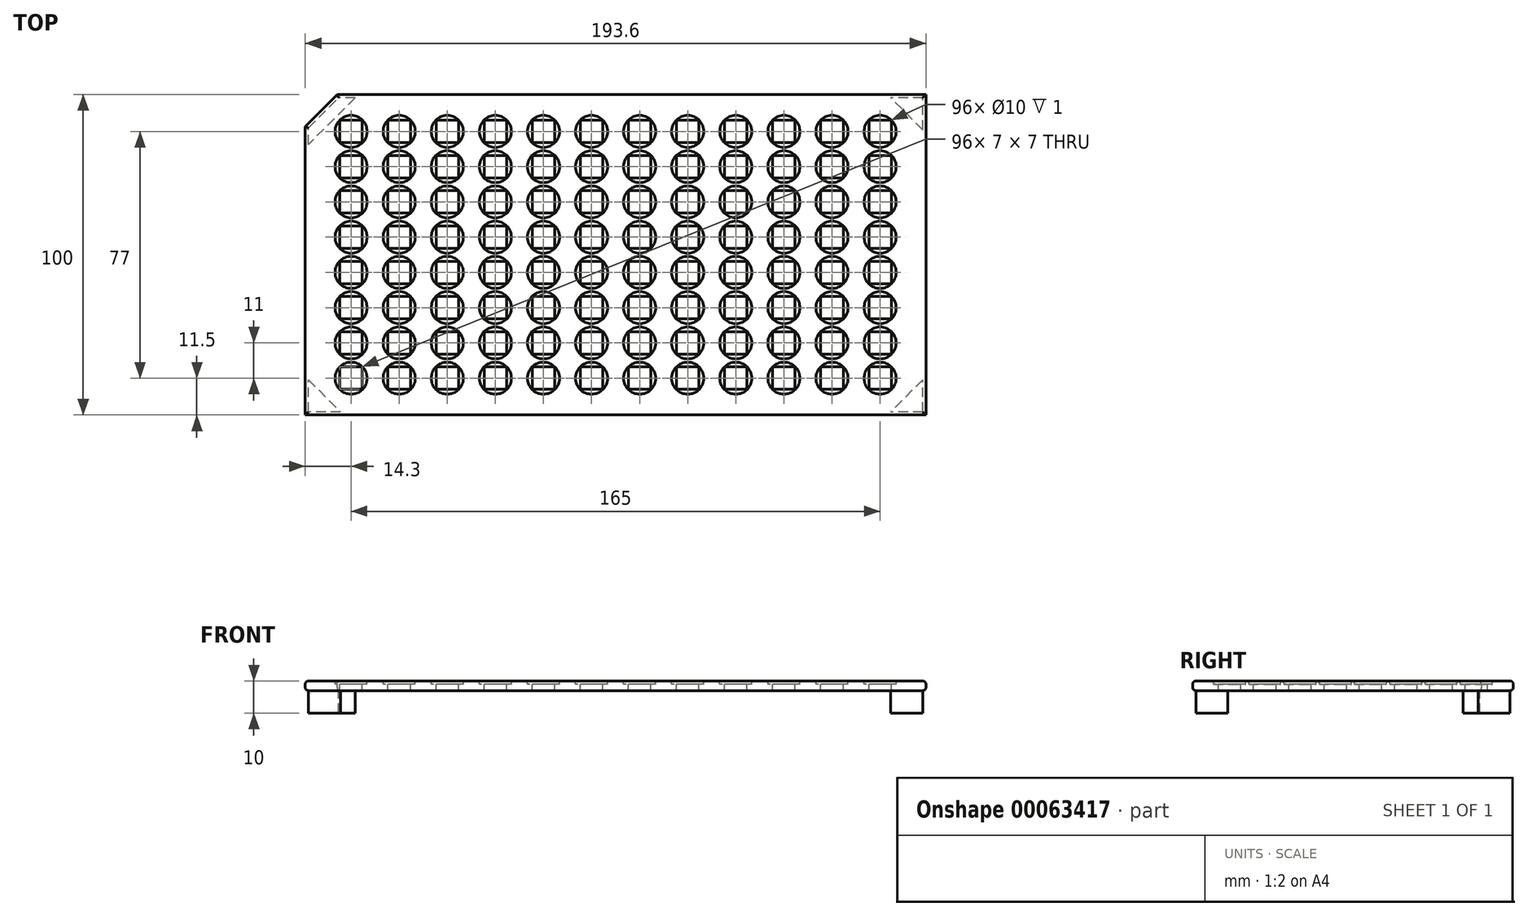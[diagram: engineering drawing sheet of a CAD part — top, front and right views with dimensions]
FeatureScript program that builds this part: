
annotation { "Feature Type Name" : "Feature", "Feature Type Description" : "" }
export const myFeature = defineFeature(function(context is Context, id is Id, definition is map)
    precondition{}
    {
        {
            var Q0;
            Q0=qCreatedBy(makeId("Top.planeOp"),FACE);
            var sketch = newSketch(context, id + "F0", { "sketchPlane" : qUnion([Q0])});
            skLineSegment(sketch, "E0.rect.bottom", {"start": v(96.8, -50) * mm, "end": v(-96.8, -50) * mm});
            skLineSegment(sketch, "E0.rect.top", {"start": v(96.8, 50) * mm, "end": v(-96.8, 50) * mm});
            skLineSegment(sketch, "E0.rect.left", {"start": v(96.8, -50) * mm, "end": v(96.8, 50) * mm});
            skLineSegment(sketch, "E0.rect.right", {"start": v(-96.8, -50) * mm, "end": v(-96.8, 50) * mm});
            skPoint(sketch, "E0.rect.middle", {"position": v(0, 0) * mm});
            skSolve(sketch);
        }
        {
            var Q0;
            Q0 = qSketchRegion(id + "F0", true);
            extrude(context, id + "F1", {"entities" : qUnion([Q0]), "depth" : 3 * mm});
        }
        {
            var Q0;
            Q0=makeQuery(id+"F1.opExtrude","CAP_FACE",FACE,{"disambiguationData":[OSD([sQuery(id+"F0.wireOp",EDGE,"E0.rect.bottom"),sQuery(id+"F0.wireOp",EDGE,"E0.rect.top"),sQuery(id+"F0.wireOp",EDGE,"E0.rect.left"),sQuery(id+"F0.wireOp",EDGE,"E0.rect.right")])],"isStart":false});
            var sketch = newSketch(context, id + "F2", { "sketchPlane" : qUnion([Q0])});
            skLineSegment(sketch, "E1.rect.bottom", {"start": v(79, 35) * mm, "end": v(86, 35) * mm});
            skLineSegment(sketch, "E1.rect.top", {"start": v(79, 42) * mm, "end": v(86, 42) * mm});
            skLineSegment(sketch, "E1.rect.left", {"start": v(79, 35) * mm, "end": v(79, 42) * mm});
            skLineSegment(sketch, "E1.rect.right", {"start": v(86, 35) * mm, "end": v(86, 42) * mm});
            skPoint(sketch, "E1.rect.middle", {"position": v(82.5, 38.5) * mm});
            skLineSegment(sketch, "E2.1.0.0", {"start": v(71, 35) * mm, "end": v(71, 42) * mm});
            skLineSegment(sketch, "E2.1.0.1", {"start": v(64, 35) * mm, "end": v(64, 42) * mm});
            skLineSegment(sketch, "E2.1.0.2", {"start": v(64, 42) * mm, "end": v(71, 42) * mm});
            skLineSegment(sketch, "E2.1.0.3", {"start": v(64, 35) * mm, "end": v(71, 35) * mm});
            skPoint(sketch, "E2.1.0.4", {"position": v(67.5, 38.5) * mm});
            skLineSegment(sketch, "E2.2.0.0", {"start": v(56, 35) * mm, "end": v(56, 42) * mm});
            skLineSegment(sketch, "E2.2.0.1", {"start": v(49, 35) * mm, "end": v(49, 42) * mm});
            skLineSegment(sketch, "E2.2.0.2", {"start": v(49, 42) * mm, "end": v(56, 42) * mm});
            skLineSegment(sketch, "E2.2.0.3", {"start": v(49, 35) * mm, "end": v(56, 35) * mm});
            skPoint(sketch, "E2.2.0.4", {"position": v(52.5, 38.5) * mm});
            skLineSegment(sketch, "E2.3.0.0", {"start": v(41, 35) * mm, "end": v(41, 42) * mm});
            skLineSegment(sketch, "E2.3.0.1", {"start": v(34, 35) * mm, "end": v(34, 42) * mm});
            skLineSegment(sketch, "E2.3.0.2", {"start": v(34, 42) * mm, "end": v(41, 42) * mm});
            skLineSegment(sketch, "E2.3.0.3", {"start": v(34, 35) * mm, "end": v(41, 35) * mm});
            skPoint(sketch, "E2.3.0.4", {"position": v(37.5, 38.5) * mm});
            skLineSegment(sketch, "E2.4.0.0", {"start": v(26, 35) * mm, "end": v(26, 42) * mm});
            skLineSegment(sketch, "E2.4.0.1", {"start": v(19, 35) * mm, "end": v(19, 42) * mm});
            skLineSegment(sketch, "E2.4.0.2", {"start": v(19, 42) * mm, "end": v(26, 42) * mm});
            skLineSegment(sketch, "E2.4.0.3", {"start": v(19, 35) * mm, "end": v(26, 35) * mm});
            skPoint(sketch, "E2.4.0.4", {"position": v(22.5, 38.5) * mm});
            skLineSegment(sketch, "E2.5.0.0", {"start": v(11, 35) * mm, "end": v(11, 42) * mm});
            skLineSegment(sketch, "E2.5.0.1", {"start": v(4, 35) * mm, "end": v(4, 42) * mm});
            skLineSegment(sketch, "E2.5.0.2", {"start": v(4, 42) * mm, "end": v(11, 42) * mm});
            skLineSegment(sketch, "E2.5.0.3", {"start": v(4, 35) * mm, "end": v(11, 35) * mm});
            skPoint(sketch, "E2.5.0.4", {"position": v(7.5, 38.5) * mm});
            skLineSegment(sketch, "E2.6.0.0", {"start": v(-4, 35) * mm, "end": v(-4, 42) * mm});
            skLineSegment(sketch, "E2.6.0.1", {"start": v(-11, 35) * mm, "end": v(-11, 42) * mm});
            skLineSegment(sketch, "E2.6.0.2", {"start": v(-11, 42) * mm, "end": v(-4, 42) * mm});
            skLineSegment(sketch, "E2.6.0.3", {"start": v(-11, 35) * mm, "end": v(-4, 35) * mm});
            skPoint(sketch, "E2.6.0.4", {"position": v(-7.5, 38.5) * mm});
            skLineSegment(sketch, "E2.7.0.0", {"start": v(-19, 35) * mm, "end": v(-19, 42) * mm});
            skLineSegment(sketch, "E2.7.0.1", {"start": v(-26, 35) * mm, "end": v(-26, 42) * mm});
            skLineSegment(sketch, "E2.7.0.2", {"start": v(-26, 42) * mm, "end": v(-19, 42) * mm});
            skLineSegment(sketch, "E2.7.0.3", {"start": v(-26, 35) * mm, "end": v(-19, 35) * mm});
            skPoint(sketch, "E2.7.0.4", {"position": v(-22.5, 38.5) * mm});
            skLineSegment(sketch, "E2.8.0.0", {"start": v(-34, 35) * mm, "end": v(-34, 42) * mm});
            skLineSegment(sketch, "E2.8.0.1", {"start": v(-41, 35) * mm, "end": v(-41, 42) * mm});
            skLineSegment(sketch, "E2.8.0.2", {"start": v(-41, 42) * mm, "end": v(-34, 42) * mm});
            skLineSegment(sketch, "E2.8.0.3", {"start": v(-41, 35) * mm, "end": v(-34, 35) * mm});
            skPoint(sketch, "E2.8.0.4", {"position": v(-37.5, 38.5) * mm});
            skLineSegment(sketch, "E2.9.0.0", {"start": v(-49, 35) * mm, "end": v(-49, 42) * mm});
            skLineSegment(sketch, "E2.9.0.1", {"start": v(-56, 35) * mm, "end": v(-56, 42) * mm});
            skLineSegment(sketch, "E2.9.0.2", {"start": v(-56, 42) * mm, "end": v(-49, 42) * mm});
            skLineSegment(sketch, "E2.9.0.3", {"start": v(-56, 35) * mm, "end": v(-49, 35) * mm});
            skPoint(sketch, "E2.9.0.4", {"position": v(-52.5, 38.5) * mm});
            skLineSegment(sketch, "E2.10.0.0", {"start": v(-64, 35) * mm, "end": v(-64, 42) * mm});
            skLineSegment(sketch, "E2.10.0.1", {"start": v(-71, 35) * mm, "end": v(-71, 42) * mm});
            skLineSegment(sketch, "E2.10.0.2", {"start": v(-71, 42) * mm, "end": v(-64, 42) * mm});
            skLineSegment(sketch, "E2.10.0.3", {"start": v(-71, 35) * mm, "end": v(-64, 35) * mm});
            skPoint(sketch, "E2.10.0.4", {"position": v(-67.5, 38.5) * mm});
            skLineSegment(sketch, "E2.11.0.0", {"start": v(-79, 35) * mm, "end": v(-79, 42) * mm});
            skLineSegment(sketch, "E2.11.0.1", {"start": v(-86, 35) * mm, "end": v(-86, 42) * mm});
            skLineSegment(sketch, "E2.11.0.2", {"start": v(-86, 42) * mm, "end": v(-79, 42) * mm});
            skLineSegment(sketch, "E2.11.0.3", {"start": v(-86, 35) * mm, "end": v(-79, 35) * mm});
            skPoint(sketch, "E2.11.0.4", {"position": v(-82.5, 38.5) * mm});
            skLineSegment(sketch, "E2.direction1", {"start": v(86, 35) * mm, "end": v(71, 35) * mm, "construction": true});
            skLineSegment(sketch, "E3.0.1.0", {"start": v(-49, 24) * mm, "end": v(-49, 31) * mm});
            skLineSegment(sketch, "E3.0.1.1", {"start": v(4, 24) * mm, "end": v(11, 24) * mm});
            skLineSegment(sketch, "E3.0.1.2", {"start": v(-56, 24) * mm, "end": v(-49, 24) * mm});
            skLineSegment(sketch, "E3.0.1.3", {"start": v(-11, 24) * mm, "end": v(-4, 24) * mm});
            skLineSegment(sketch, "E3.0.1.4", {"start": v(-71, 24) * mm, "end": v(-64, 24) * mm});
            skPoint(sketch, "E3.0.1.5", {"position": v(7.5, 27.5) * mm});
            skLineSegment(sketch, "E3.0.1.6", {"start": v(-26, 24) * mm, "end": v(-26, 31) * mm});
            skLineSegment(sketch, "E3.0.1.7", {"start": v(11, 24) * mm, "end": v(11, 31) * mm});
            skPoint(sketch, "E3.0.1.8", {"position": v(-52.5, 27.5) * mm});
            skLineSegment(sketch, "E3.0.1.9", {"start": v(-86, 24) * mm, "end": v(-86, 31) * mm});
            skLineSegment(sketch, "E3.0.1.10", {"start": v(-34, 24) * mm, "end": v(-34, 31) * mm});
            skLineSegment(sketch, "E3.0.1.11", {"start": v(26, 24) * mm, "end": v(26, 31) * mm});
            skPoint(sketch, "E3.0.1.12", {"position": v(37.5, 27.5) * mm});
            skLineSegment(sketch, "E3.0.1.13", {"start": v(-79, 24) * mm, "end": v(-79, 31) * mm});
            skLineSegment(sketch, "E3.0.1.14", {"start": v(-19, 24) * mm, "end": v(-19, 31) * mm});
            skPoint(sketch, "E3.0.1.15", {"position": v(-82.5, 27.5) * mm});
            skPoint(sketch, "E3.0.1.16", {"position": v(52.5, 27.5) * mm});
            skLineSegment(sketch, "E3.0.1.17", {"start": v(-64, 24) * mm, "end": v(-64, 31) * mm});
            skLineSegment(sketch, "E3.0.1.18", {"start": v(-4, 24) * mm, "end": v(-4, 31) * mm});
            skLineSegment(sketch, "E3.0.1.19", {"start": v(-56, 24) * mm, "end": v(-56, 31) * mm});
            skLineSegment(sketch, "E3.0.1.20", {"start": v(-26, 31) * mm, "end": v(-19, 31) * mm});
            skLineSegment(sketch, "E3.0.1.21", {"start": v(4, 24) * mm, "end": v(4, 31) * mm});
            skPoint(sketch, "E3.0.1.22", {"position": v(-67.5, 27.5) * mm});
            skLineSegment(sketch, "E3.0.1.23", {"start": v(-86, 31) * mm, "end": v(-79, 31) * mm});
            skLineSegment(sketch, "E3.0.1.24", {"start": v(-41, 24) * mm, "end": v(-41, 31) * mm});
            skLineSegment(sketch, "E3.0.1.25", {"start": v(19, 24) * mm, "end": v(19, 31) * mm});
            skPoint(sketch, "E3.0.1.26", {"position": v(-7.5, 27.5) * mm});
            skPoint(sketch, "E3.0.1.27", {"position": v(22.5, 27.5) * mm});
            skLineSegment(sketch, "E3.0.1.28", {"start": v(34, 24) * mm, "end": v(34, 31) * mm});
            skLineSegment(sketch, "E3.0.1.29", {"start": v(34, 31) * mm, "end": v(41, 31) * mm});
            skLineSegment(sketch, "E3.0.1.30", {"start": v(34, 24) * mm, "end": v(41, 24) * mm});
            skPoint(sketch, "E3.0.1.31", {"position": v(82.5, 27.5) * mm});
            skLineSegment(sketch, "E3.0.1.32", {"start": v(79, 24) * mm, "end": v(86, 24) * mm});
            skLineSegment(sketch, "E3.0.1.33", {"start": v(79, 31) * mm, "end": v(86, 31) * mm});
            skLineSegment(sketch, "E3.0.1.34", {"start": v(79, 24) * mm, "end": v(79, 31) * mm});
            skLineSegment(sketch, "E3.0.1.35", {"start": v(86, 24) * mm, "end": v(86, 31) * mm});
            skLineSegment(sketch, "E3.0.1.36", {"start": v(71, 24) * mm, "end": v(71, 31) * mm});
            skLineSegment(sketch, "E3.0.1.37", {"start": v(64, 24) * mm, "end": v(64, 31) * mm});
            skLineSegment(sketch, "E3.0.1.38", {"start": v(64, 31) * mm, "end": v(71, 31) * mm});
            skLineSegment(sketch, "E3.0.1.39", {"start": v(64, 24) * mm, "end": v(71, 24) * mm});
            skLineSegment(sketch, "E3.0.1.40", {"start": v(56, 24) * mm, "end": v(56, 31) * mm});
            skLineSegment(sketch, "E3.0.1.41", {"start": v(49, 24) * mm, "end": v(49, 31) * mm});
            skLineSegment(sketch, "E3.0.1.42", {"start": v(49, 31) * mm, "end": v(56, 31) * mm});
            skLineSegment(sketch, "E3.0.1.43", {"start": v(49, 24) * mm, "end": v(56, 24) * mm});
            skLineSegment(sketch, "E3.0.1.44", {"start": v(-71, 24) * mm, "end": v(-71, 31) * mm});
            skLineSegment(sketch, "E3.0.1.45", {"start": v(-11, 24) * mm, "end": v(-11, 31) * mm});
            skLineSegment(sketch, "E3.0.1.46", {"start": v(41, 24) * mm, "end": v(41, 31) * mm});
            skLineSegment(sketch, "E3.0.1.47", {"start": v(-26, 24) * mm, "end": v(-19, 24) * mm});
            skLineSegment(sketch, "E3.0.1.48", {"start": v(-56, 31) * mm, "end": v(-49, 31) * mm});
            skLineSegment(sketch, "E3.0.1.49", {"start": v(4, 31) * mm, "end": v(11, 31) * mm});
            skLineSegment(sketch, "E3.0.1.50", {"start": v(-86, 24) * mm, "end": v(-79, 24) * mm});
            skLineSegment(sketch, "E3.0.1.51", {"start": v(-41, 31) * mm, "end": v(-34, 31) * mm});
            skLineSegment(sketch, "E3.0.1.52", {"start": v(19, 31) * mm, "end": v(26, 31) * mm});
            skPoint(sketch, "E3.0.1.53", {"position": v(-22.5, 27.5) * mm});
            skPoint(sketch, "E3.0.1.54", {"position": v(67.5, 27.5) * mm});
            skLineSegment(sketch, "E3.0.1.55", {"start": v(-71, 31) * mm, "end": v(-64, 31) * mm});
            skLineSegment(sketch, "E3.0.1.56", {"start": v(-11, 31) * mm, "end": v(-4, 31) * mm});
            skLineSegment(sketch, "E3.0.1.57", {"start": v(-41, 24) * mm, "end": v(-34, 24) * mm});
            skLineSegment(sketch, "E3.0.1.58", {"start": v(19, 24) * mm, "end": v(26, 24) * mm});
            skPoint(sketch, "E3.0.1.59", {"position": v(-37.5, 27.5) * mm});
            skLineSegment(sketch, "E3.0.1.60", {"start": v(86, 24) * mm, "end": v(71, 24) * mm, "construction": true});
            skLineSegment(sketch, "E3.0.2.0", {"start": v(-49, 13) * mm, "end": v(-49, 20) * mm});
            skLineSegment(sketch, "E3.0.2.1", {"start": v(4, 13) * mm, "end": v(11, 13) * mm});
            skLineSegment(sketch, "E3.0.2.2", {"start": v(-56, 13) * mm, "end": v(-49, 13) * mm});
            skLineSegment(sketch, "E3.0.2.3", {"start": v(-11, 13) * mm, "end": v(-4, 13) * mm});
            skLineSegment(sketch, "E3.0.2.4", {"start": v(-71, 13) * mm, "end": v(-64, 13) * mm});
            skPoint(sketch, "E3.0.2.5", {"position": v(7.5, 16.5) * mm});
            skLineSegment(sketch, "E3.0.2.6", {"start": v(-26, 13) * mm, "end": v(-26, 20) * mm});
            skLineSegment(sketch, "E3.0.2.7", {"start": v(11, 13) * mm, "end": v(11, 20) * mm});
            skPoint(sketch, "E3.0.2.8", {"position": v(-52.5, 16.5) * mm});
            skLineSegment(sketch, "E3.0.2.9", {"start": v(-86, 13) * mm, "end": v(-86, 20) * mm});
            skLineSegment(sketch, "E3.0.2.10", {"start": v(-34, 13) * mm, "end": v(-34, 20) * mm});
            skLineSegment(sketch, "E3.0.2.11", {"start": v(26, 13) * mm, "end": v(26, 20) * mm});
            skPoint(sketch, "E3.0.2.12", {"position": v(37.5, 16.5) * mm});
            skLineSegment(sketch, "E3.0.2.13", {"start": v(-79, 13) * mm, "end": v(-79, 20) * mm});
            skLineSegment(sketch, "E3.0.2.14", {"start": v(-19, 13) * mm, "end": v(-19, 20) * mm});
            skPoint(sketch, "E3.0.2.15", {"position": v(-82.5, 16.5) * mm});
            skPoint(sketch, "E3.0.2.16", {"position": v(52.5, 16.5) * mm});
            skLineSegment(sketch, "E3.0.2.17", {"start": v(-64, 13) * mm, "end": v(-64, 20) * mm});
            skLineSegment(sketch, "E3.0.2.18", {"start": v(-4, 13) * mm, "end": v(-4, 20) * mm});
            skLineSegment(sketch, "E3.0.2.19", {"start": v(-56, 13) * mm, "end": v(-56, 20) * mm});
            skLineSegment(sketch, "E3.0.2.20", {"start": v(-26, 20) * mm, "end": v(-19, 20) * mm});
            skLineSegment(sketch, "E3.0.2.21", {"start": v(4, 13) * mm, "end": v(4, 20) * mm});
            skPoint(sketch, "E3.0.2.22", {"position": v(-67.5, 16.5) * mm});
            skLineSegment(sketch, "E3.0.2.23", {"start": v(-86, 20) * mm, "end": v(-79, 20) * mm});
            skLineSegment(sketch, "E3.0.2.24", {"start": v(-41, 13) * mm, "end": v(-41, 20) * mm});
            skLineSegment(sketch, "E3.0.2.25", {"start": v(19, 13) * mm, "end": v(19, 20) * mm});
            skPoint(sketch, "E3.0.2.26", {"position": v(-7.5, 16.5) * mm});
            skPoint(sketch, "E3.0.2.27", {"position": v(22.5, 16.5) * mm});
            skLineSegment(sketch, "E3.0.2.28", {"start": v(34, 13) * mm, "end": v(34, 20) * mm});
            skLineSegment(sketch, "E3.0.2.29", {"start": v(34, 20) * mm, "end": v(41, 20) * mm});
            skLineSegment(sketch, "E3.0.2.30", {"start": v(34, 13) * mm, "end": v(41, 13) * mm});
            skPoint(sketch, "E3.0.2.31", {"position": v(82.5, 16.5) * mm});
            skLineSegment(sketch, "E3.0.2.32", {"start": v(79, 13) * mm, "end": v(86, 13) * mm});
            skLineSegment(sketch, "E3.0.2.33", {"start": v(79, 20) * mm, "end": v(86, 20) * mm});
            skLineSegment(sketch, "E3.0.2.34", {"start": v(79, 13) * mm, "end": v(79, 20) * mm});
            skLineSegment(sketch, "E3.0.2.35", {"start": v(86, 13) * mm, "end": v(86, 20) * mm});
            skLineSegment(sketch, "E3.0.2.36", {"start": v(71, 13) * mm, "end": v(71, 20) * mm});
            skLineSegment(sketch, "E3.0.2.37", {"start": v(64, 13) * mm, "end": v(64, 20) * mm});
            skLineSegment(sketch, "E3.0.2.38", {"start": v(64, 20) * mm, "end": v(71, 20) * mm});
            skLineSegment(sketch, "E3.0.2.39", {"start": v(64, 13) * mm, "end": v(71, 13) * mm});
            skLineSegment(sketch, "E3.0.2.40", {"start": v(56, 13) * mm, "end": v(56, 20) * mm});
            skLineSegment(sketch, "E3.0.2.41", {"start": v(49, 13) * mm, "end": v(49, 20) * mm});
            skLineSegment(sketch, "E3.0.2.42", {"start": v(49, 20) * mm, "end": v(56, 20) * mm});
            skLineSegment(sketch, "E3.0.2.43", {"start": v(49, 13) * mm, "end": v(56, 13) * mm});
            skLineSegment(sketch, "E3.0.2.44", {"start": v(-71, 13) * mm, "end": v(-71, 20) * mm});
            skLineSegment(sketch, "E3.0.2.45", {"start": v(-11, 13) * mm, "end": v(-11, 20) * mm});
            skLineSegment(sketch, "E3.0.2.46", {"start": v(41, 13) * mm, "end": v(41, 20) * mm});
            skLineSegment(sketch, "E3.0.2.47", {"start": v(-26, 13) * mm, "end": v(-19, 13) * mm});
            skLineSegment(sketch, "E3.0.2.48", {"start": v(-56, 20) * mm, "end": v(-49, 20) * mm});
            skLineSegment(sketch, "E3.0.2.49", {"start": v(4, 20) * mm, "end": v(11, 20) * mm});
            skLineSegment(sketch, "E3.0.2.50", {"start": v(-86, 13) * mm, "end": v(-79, 13) * mm});
            skLineSegment(sketch, "E3.0.2.51", {"start": v(-41, 20) * mm, "end": v(-34, 20) * mm});
            skLineSegment(sketch, "E3.0.2.52", {"start": v(19, 20) * mm, "end": v(26, 20) * mm});
            skPoint(sketch, "E3.0.2.53", {"position": v(-22.5, 16.5) * mm});
            skPoint(sketch, "E3.0.2.54", {"position": v(67.5, 16.5) * mm});
            skLineSegment(sketch, "E3.0.2.55", {"start": v(-71, 20) * mm, "end": v(-64, 20) * mm});
            skLineSegment(sketch, "E3.0.2.56", {"start": v(-11, 20) * mm, "end": v(-4, 20) * mm});
            skLineSegment(sketch, "E3.0.2.57", {"start": v(-41, 13) * mm, "end": v(-34, 13) * mm});
            skLineSegment(sketch, "E3.0.2.58", {"start": v(19, 13) * mm, "end": v(26, 13) * mm});
            skPoint(sketch, "E3.0.2.59", {"position": v(-37.5, 16.5) * mm});
            skLineSegment(sketch, "E3.0.2.60", {"start": v(86, 13) * mm, "end": v(71, 13) * mm, "construction": true});
            skLineSegment(sketch, "E3.0.3.0", {"start": v(-49, 2) * mm, "end": v(-49, 9) * mm});
            skLineSegment(sketch, "E3.0.3.1", {"start": v(4, 2) * mm, "end": v(11, 2) * mm});
            skLineSegment(sketch, "E3.0.3.2", {"start": v(-56, 2) * mm, "end": v(-49, 2) * mm});
            skLineSegment(sketch, "E3.0.3.3", {"start": v(-11, 2) * mm, "end": v(-4, 2) * mm});
            skLineSegment(sketch, "E3.0.3.4", {"start": v(-71, 2) * mm, "end": v(-64, 2) * mm});
            skPoint(sketch, "E3.0.3.5", {"position": v(7.5, 5.5) * mm});
            skLineSegment(sketch, "E3.0.3.6", {"start": v(-26, 2) * mm, "end": v(-26, 9) * mm});
            skLineSegment(sketch, "E3.0.3.7", {"start": v(11, 2) * mm, "end": v(11, 9) * mm});
            skPoint(sketch, "E3.0.3.8", {"position": v(-52.5, 5.5) * mm});
            skLineSegment(sketch, "E3.0.3.9", {"start": v(-86, 2) * mm, "end": v(-86, 9) * mm});
            skLineSegment(sketch, "E3.0.3.10", {"start": v(-34, 2) * mm, "end": v(-34, 9) * mm});
            skLineSegment(sketch, "E3.0.3.11", {"start": v(26, 2) * mm, "end": v(26, 9) * mm});
            skPoint(sketch, "E3.0.3.12", {"position": v(37.5, 5.5) * mm});
            skLineSegment(sketch, "E3.0.3.13", {"start": v(-79, 2) * mm, "end": v(-79, 9) * mm});
            skLineSegment(sketch, "E3.0.3.14", {"start": v(-19, 2) * mm, "end": v(-19, 9) * mm});
            skPoint(sketch, "E3.0.3.15", {"position": v(-82.5, 5.5) * mm});
            skPoint(sketch, "E3.0.3.16", {"position": v(52.5, 5.5) * mm});
            skLineSegment(sketch, "E3.0.3.17", {"start": v(-64, 2) * mm, "end": v(-64, 9) * mm});
            skLineSegment(sketch, "E3.0.3.18", {"start": v(-4, 2) * mm, "end": v(-4, 9) * mm});
            skLineSegment(sketch, "E3.0.3.19", {"start": v(-56, 2) * mm, "end": v(-56, 9) * mm});
            skLineSegment(sketch, "E3.0.3.20", {"start": v(-26, 9) * mm, "end": v(-19, 9) * mm});
            skLineSegment(sketch, "E3.0.3.21", {"start": v(4, 2) * mm, "end": v(4, 9) * mm});
            skPoint(sketch, "E3.0.3.22", {"position": v(-67.5, 5.5) * mm});
            skLineSegment(sketch, "E3.0.3.23", {"start": v(-86, 9) * mm, "end": v(-79, 9) * mm});
            skLineSegment(sketch, "E3.0.3.24", {"start": v(-41, 2) * mm, "end": v(-41, 9) * mm});
            skLineSegment(sketch, "E3.0.3.25", {"start": v(19, 2) * mm, "end": v(19, 9) * mm});
            skPoint(sketch, "E3.0.3.26", {"position": v(-7.5, 5.5) * mm});
            skPoint(sketch, "E3.0.3.27", {"position": v(22.5, 5.5) * mm});
            skLineSegment(sketch, "E3.0.3.28", {"start": v(34, 2) * mm, "end": v(34, 9) * mm});
            skLineSegment(sketch, "E3.0.3.29", {"start": v(34, 9) * mm, "end": v(41, 9) * mm});
            skLineSegment(sketch, "E3.0.3.30", {"start": v(34, 2) * mm, "end": v(41, 2) * mm});
            skPoint(sketch, "E3.0.3.31", {"position": v(82.5, 5.5) * mm});
            skLineSegment(sketch, "E3.0.3.32", {"start": v(79, 2) * mm, "end": v(86, 2) * mm});
            skLineSegment(sketch, "E3.0.3.33", {"start": v(79, 9) * mm, "end": v(86, 9) * mm});
            skLineSegment(sketch, "E3.0.3.34", {"start": v(79, 2) * mm, "end": v(79, 9) * mm});
            skLineSegment(sketch, "E3.0.3.35", {"start": v(86, 2) * mm, "end": v(86, 9) * mm});
            skLineSegment(sketch, "E3.0.3.36", {"start": v(71, 2) * mm, "end": v(71, 9) * mm});
            skLineSegment(sketch, "E3.0.3.37", {"start": v(64, 2) * mm, "end": v(64, 9) * mm});
            skLineSegment(sketch, "E3.0.3.38", {"start": v(64, 9) * mm, "end": v(71, 9) * mm});
            skLineSegment(sketch, "E3.0.3.39", {"start": v(64, 2) * mm, "end": v(71, 2) * mm});
            skLineSegment(sketch, "E3.0.3.40", {"start": v(56, 2) * mm, "end": v(56, 9) * mm});
            skLineSegment(sketch, "E3.0.3.41", {"start": v(49, 2) * mm, "end": v(49, 9) * mm});
            skLineSegment(sketch, "E3.0.3.42", {"start": v(49, 9) * mm, "end": v(56, 9) * mm});
            skLineSegment(sketch, "E3.0.3.43", {"start": v(49, 2) * mm, "end": v(56, 2) * mm});
            skLineSegment(sketch, "E3.0.3.44", {"start": v(-71, 2) * mm, "end": v(-71, 9) * mm});
            skLineSegment(sketch, "E3.0.3.45", {"start": v(-11, 2) * mm, "end": v(-11, 9) * mm});
            skLineSegment(sketch, "E3.0.3.46", {"start": v(41, 2) * mm, "end": v(41, 9) * mm});
            skLineSegment(sketch, "E3.0.3.47", {"start": v(-26, 2) * mm, "end": v(-19, 2) * mm});
            skLineSegment(sketch, "E3.0.3.48", {"start": v(-56, 9) * mm, "end": v(-49, 9) * mm});
            skLineSegment(sketch, "E3.0.3.49", {"start": v(4, 9) * mm, "end": v(11, 9) * mm});
            skLineSegment(sketch, "E3.0.3.50", {"start": v(-86, 2) * mm, "end": v(-79, 2) * mm});
            skLineSegment(sketch, "E3.0.3.51", {"start": v(-41, 9) * mm, "end": v(-34, 9) * mm});
            skLineSegment(sketch, "E3.0.3.52", {"start": v(19, 9) * mm, "end": v(26, 9) * mm});
            skPoint(sketch, "E3.0.3.53", {"position": v(-22.5, 5.5) * mm});
            skPoint(sketch, "E3.0.3.54", {"position": v(67.5, 5.5) * mm});
            skLineSegment(sketch, "E3.0.3.55", {"start": v(-71, 9) * mm, "end": v(-64, 9) * mm});
            skLineSegment(sketch, "E3.0.3.56", {"start": v(-11, 9) * mm, "end": v(-4, 9) * mm});
            skLineSegment(sketch, "E3.0.3.57", {"start": v(-41, 2) * mm, "end": v(-34, 2) * mm});
            skLineSegment(sketch, "E3.0.3.58", {"start": v(19, 2) * mm, "end": v(26, 2) * mm});
            skPoint(sketch, "E3.0.3.59", {"position": v(-37.5, 5.5) * mm});
            skLineSegment(sketch, "E3.0.3.60", {"start": v(86, 2) * mm, "end": v(71, 2) * mm, "construction": true});
            skLineSegment(sketch, "E3.0.4.0", {"start": v(-49, -9) * mm, "end": v(-49, -2) * mm});
            skLineSegment(sketch, "E3.0.4.1", {"start": v(4, -9) * mm, "end": v(11, -9) * mm});
            skLineSegment(sketch, "E3.0.4.2", {"start": v(-56, -9) * mm, "end": v(-49, -9) * mm});
            skLineSegment(sketch, "E3.0.4.3", {"start": v(-11, -9) * mm, "end": v(-4, -9) * mm});
            skLineSegment(sketch, "E3.0.4.4", {"start": v(-71, -9) * mm, "end": v(-64, -9) * mm});
            skPoint(sketch, "E3.0.4.5", {"position": v(7.5, -5.5) * mm});
            skLineSegment(sketch, "E3.0.4.6", {"start": v(-26, -9) * mm, "end": v(-26, -2) * mm});
            skLineSegment(sketch, "E3.0.4.7", {"start": v(11, -9) * mm, "end": v(11, -2) * mm});
            skPoint(sketch, "E3.0.4.8", {"position": v(-52.5, -5.5) * mm});
            skLineSegment(sketch, "E3.0.4.9", {"start": v(-86, -9) * mm, "end": v(-86, -2) * mm});
            skLineSegment(sketch, "E3.0.4.10", {"start": v(-34, -9) * mm, "end": v(-34, -2) * mm});
            skLineSegment(sketch, "E3.0.4.11", {"start": v(26, -9) * mm, "end": v(26, -2) * mm});
            skPoint(sketch, "E3.0.4.12", {"position": v(37.5, -5.5) * mm});
            skLineSegment(sketch, "E3.0.4.13", {"start": v(-79, -9) * mm, "end": v(-79, -2) * mm});
            skLineSegment(sketch, "E3.0.4.14", {"start": v(-19, -9) * mm, "end": v(-19, -2) * mm});
            skPoint(sketch, "E3.0.4.15", {"position": v(-82.5, -5.5) * mm});
            skPoint(sketch, "E3.0.4.16", {"position": v(52.5, -5.5) * mm});
            skLineSegment(sketch, "E3.0.4.17", {"start": v(-64, -9) * mm, "end": v(-64, -2) * mm});
            skLineSegment(sketch, "E3.0.4.18", {"start": v(-4, -9) * mm, "end": v(-4, -2) * mm});
            skLineSegment(sketch, "E3.0.4.19", {"start": v(-56, -9) * mm, "end": v(-56, -2) * mm});
            skLineSegment(sketch, "E3.0.4.20", {"start": v(-26, -2) * mm, "end": v(-19, -2) * mm});
            skLineSegment(sketch, "E3.0.4.21", {"start": v(4, -9) * mm, "end": v(4, -2) * mm});
            skPoint(sketch, "E3.0.4.22", {"position": v(-67.5, -5.5) * mm});
            skLineSegment(sketch, "E3.0.4.23", {"start": v(-86, -2) * mm, "end": v(-79, -2) * mm});
            skLineSegment(sketch, "E3.0.4.24", {"start": v(-41, -9) * mm, "end": v(-41, -2) * mm});
            skLineSegment(sketch, "E3.0.4.25", {"start": v(19, -9) * mm, "end": v(19, -2) * mm});
            skPoint(sketch, "E3.0.4.26", {"position": v(-7.5, -5.5) * mm});
            skPoint(sketch, "E3.0.4.27", {"position": v(22.5, -5.5) * mm});
            skLineSegment(sketch, "E3.0.4.28", {"start": v(34, -9) * mm, "end": v(34, -2) * mm});
            skLineSegment(sketch, "E3.0.4.29", {"start": v(34, -2) * mm, "end": v(41, -2) * mm});
            skLineSegment(sketch, "E3.0.4.30", {"start": v(34, -9) * mm, "end": v(41, -9) * mm});
            skPoint(sketch, "E3.0.4.31", {"position": v(82.5, -5.5) * mm});
            skLineSegment(sketch, "E3.0.4.32", {"start": v(79, -9) * mm, "end": v(86, -9) * mm});
            skLineSegment(sketch, "E3.0.4.33", {"start": v(79, -2) * mm, "end": v(86, -2) * mm});
            skLineSegment(sketch, "E3.0.4.34", {"start": v(79, -9) * mm, "end": v(79, -2) * mm});
            skLineSegment(sketch, "E3.0.4.35", {"start": v(86, -9) * mm, "end": v(86, -2) * mm});
            skLineSegment(sketch, "E3.0.4.36", {"start": v(71, -9) * mm, "end": v(71, -2) * mm});
            skLineSegment(sketch, "E3.0.4.37", {"start": v(64, -9) * mm, "end": v(64, -2) * mm});
            skLineSegment(sketch, "E3.0.4.38", {"start": v(64, -2) * mm, "end": v(71, -2) * mm});
            skLineSegment(sketch, "E3.0.4.39", {"start": v(64, -9) * mm, "end": v(71, -9) * mm});
            skLineSegment(sketch, "E3.0.4.40", {"start": v(56, -9) * mm, "end": v(56, -2) * mm});
            skLineSegment(sketch, "E3.0.4.41", {"start": v(49, -9) * mm, "end": v(49, -2) * mm});
            skLineSegment(sketch, "E3.0.4.42", {"start": v(49, -2) * mm, "end": v(56, -2) * mm});
            skLineSegment(sketch, "E3.0.4.43", {"start": v(49, -9) * mm, "end": v(56, -9) * mm});
            skLineSegment(sketch, "E3.0.4.44", {"start": v(-71, -9) * mm, "end": v(-71, -2) * mm});
            skLineSegment(sketch, "E3.0.4.45", {"start": v(-11, -9) * mm, "end": v(-11, -2) * mm});
            skLineSegment(sketch, "E3.0.4.46", {"start": v(41, -9) * mm, "end": v(41, -2) * mm});
            skLineSegment(sketch, "E3.0.4.47", {"start": v(-26, -9) * mm, "end": v(-19, -9) * mm});
            skLineSegment(sketch, "E3.0.4.48", {"start": v(-56, -2) * mm, "end": v(-49, -2) * mm});
            skLineSegment(sketch, "E3.0.4.49", {"start": v(4, -2) * mm, "end": v(11, -2) * mm});
            skLineSegment(sketch, "E3.0.4.50", {"start": v(-86, -9) * mm, "end": v(-79, -9) * mm});
            skLineSegment(sketch, "E3.0.4.51", {"start": v(-41, -2) * mm, "end": v(-34, -2) * mm});
            skLineSegment(sketch, "E3.0.4.52", {"start": v(19, -2) * mm, "end": v(26, -2) * mm});
            skPoint(sketch, "E3.0.4.53", {"position": v(-22.5, -5.5) * mm});
            skPoint(sketch, "E3.0.4.54", {"position": v(67.5, -5.5) * mm});
            skLineSegment(sketch, "E3.0.4.55", {"start": v(-71, -2) * mm, "end": v(-64, -2) * mm});
            skLineSegment(sketch, "E3.0.4.56", {"start": v(-11, -2) * mm, "end": v(-4, -2) * mm});
            skLineSegment(sketch, "E3.0.4.57", {"start": v(-41, -9) * mm, "end": v(-34, -9) * mm});
            skLineSegment(sketch, "E3.0.4.58", {"start": v(19, -9) * mm, "end": v(26, -9) * mm});
            skPoint(sketch, "E3.0.4.59", {"position": v(-37.5, -5.5) * mm});
            skLineSegment(sketch, "E3.0.4.60", {"start": v(86, -9) * mm, "end": v(71, -9) * mm, "construction": true});
            skLineSegment(sketch, "E3.0.5.0", {"start": v(-49, -20) * mm, "end": v(-49, -13) * mm});
            skLineSegment(sketch, "E3.0.5.1", {"start": v(4, -20) * mm, "end": v(11, -20) * mm});
            skLineSegment(sketch, "E3.0.5.2", {"start": v(-56, -20) * mm, "end": v(-49, -20) * mm});
            skLineSegment(sketch, "E3.0.5.3", {"start": v(-11, -20) * mm, "end": v(-4, -20) * mm});
            skLineSegment(sketch, "E3.0.5.4", {"start": v(-71, -20) * mm, "end": v(-64, -20) * mm});
            skPoint(sketch, "E3.0.5.5", {"position": v(7.5, -16.5) * mm});
            skLineSegment(sketch, "E3.0.5.6", {"start": v(-26, -20) * mm, "end": v(-26, -13) * mm});
            skLineSegment(sketch, "E3.0.5.7", {"start": v(11, -20) * mm, "end": v(11, -13) * mm});
            skPoint(sketch, "E3.0.5.8", {"position": v(-52.5, -16.5) * mm});
            skLineSegment(sketch, "E3.0.5.9", {"start": v(-86, -20) * mm, "end": v(-86, -13) * mm});
            skLineSegment(sketch, "E3.0.5.10", {"start": v(-34, -20) * mm, "end": v(-34, -13) * mm});
            skLineSegment(sketch, "E3.0.5.11", {"start": v(26, -20) * mm, "end": v(26, -13) * mm});
            skPoint(sketch, "E3.0.5.12", {"position": v(37.5, -16.5) * mm});
            skLineSegment(sketch, "E3.0.5.13", {"start": v(-79, -20) * mm, "end": v(-79, -13) * mm});
            skLineSegment(sketch, "E3.0.5.14", {"start": v(-19, -20) * mm, "end": v(-19, -13) * mm});
            skPoint(sketch, "E3.0.5.15", {"position": v(-82.5, -16.5) * mm});
            skPoint(sketch, "E3.0.5.16", {"position": v(52.5, -16.5) * mm});
            skLineSegment(sketch, "E3.0.5.17", {"start": v(-64, -20) * mm, "end": v(-64, -13) * mm});
            skLineSegment(sketch, "E3.0.5.18", {"start": v(-4, -20) * mm, "end": v(-4, -13) * mm});
            skLineSegment(sketch, "E3.0.5.19", {"start": v(-56, -20) * mm, "end": v(-56, -13) * mm});
            skLineSegment(sketch, "E3.0.5.20", {"start": v(-26, -13) * mm, "end": v(-19, -13) * mm});
            skLineSegment(sketch, "E3.0.5.21", {"start": v(4, -20) * mm, "end": v(4, -13) * mm});
            skPoint(sketch, "E3.0.5.22", {"position": v(-67.5, -16.5) * mm});
            skLineSegment(sketch, "E3.0.5.23", {"start": v(-86, -13) * mm, "end": v(-79, -13) * mm});
            skLineSegment(sketch, "E3.0.5.24", {"start": v(-41, -20) * mm, "end": v(-41, -13) * mm});
            skLineSegment(sketch, "E3.0.5.25", {"start": v(19, -20) * mm, "end": v(19, -13) * mm});
            skPoint(sketch, "E3.0.5.26", {"position": v(-7.5, -16.5) * mm});
            skPoint(sketch, "E3.0.5.27", {"position": v(22.5, -16.5) * mm});
            skLineSegment(sketch, "E3.0.5.28", {"start": v(34, -20) * mm, "end": v(34, -13) * mm});
            skLineSegment(sketch, "E3.0.5.29", {"start": v(34, -13) * mm, "end": v(41, -13) * mm});
            skLineSegment(sketch, "E3.0.5.30", {"start": v(34, -20) * mm, "end": v(41, -20) * mm});
            skPoint(sketch, "E3.0.5.31", {"position": v(82.5, -16.5) * mm});
            skLineSegment(sketch, "E3.0.5.32", {"start": v(79, -20) * mm, "end": v(86, -20) * mm});
            skLineSegment(sketch, "E3.0.5.33", {"start": v(79, -13) * mm, "end": v(86, -13) * mm});
            skLineSegment(sketch, "E3.0.5.34", {"start": v(79, -20) * mm, "end": v(79, -13) * mm});
            skLineSegment(sketch, "E3.0.5.35", {"start": v(86, -20) * mm, "end": v(86, -13) * mm});
            skLineSegment(sketch, "E3.0.5.36", {"start": v(71, -20) * mm, "end": v(71, -13) * mm});
            skLineSegment(sketch, "E3.0.5.37", {"start": v(64, -20) * mm, "end": v(64, -13) * mm});
            skLineSegment(sketch, "E3.0.5.38", {"start": v(64, -13) * mm, "end": v(71, -13) * mm});
            skLineSegment(sketch, "E3.0.5.39", {"start": v(64, -20) * mm, "end": v(71, -20) * mm});
            skLineSegment(sketch, "E3.0.5.40", {"start": v(56, -20) * mm, "end": v(56, -13) * mm});
            skLineSegment(sketch, "E3.0.5.41", {"start": v(49, -20) * mm, "end": v(49, -13) * mm});
            skLineSegment(sketch, "E3.0.5.42", {"start": v(49, -13) * mm, "end": v(56, -13) * mm});
            skLineSegment(sketch, "E3.0.5.43", {"start": v(49, -20) * mm, "end": v(56, -20) * mm});
            skLineSegment(sketch, "E3.0.5.44", {"start": v(-71, -20) * mm, "end": v(-71, -13) * mm});
            skLineSegment(sketch, "E3.0.5.45", {"start": v(-11, -20) * mm, "end": v(-11, -13) * mm});
            skLineSegment(sketch, "E3.0.5.46", {"start": v(41, -20) * mm, "end": v(41, -13) * mm});
            skLineSegment(sketch, "E3.0.5.47", {"start": v(-26, -20) * mm, "end": v(-19, -20) * mm});
            skLineSegment(sketch, "E3.0.5.48", {"start": v(-56, -13) * mm, "end": v(-49, -13) * mm});
            skLineSegment(sketch, "E3.0.5.49", {"start": v(4, -13) * mm, "end": v(11, -13) * mm});
            skLineSegment(sketch, "E3.0.5.50", {"start": v(-86, -20) * mm, "end": v(-79, -20) * mm});
            skLineSegment(sketch, "E3.0.5.51", {"start": v(-41, -13) * mm, "end": v(-34, -13) * mm});
            skLineSegment(sketch, "E3.0.5.52", {"start": v(19, -13) * mm, "end": v(26, -13) * mm});
            skPoint(sketch, "E3.0.5.53", {"position": v(-22.5, -16.5) * mm});
            skPoint(sketch, "E3.0.5.54", {"position": v(67.5, -16.5) * mm});
            skLineSegment(sketch, "E3.0.5.55", {"start": v(-71, -13) * mm, "end": v(-64, -13) * mm});
            skLineSegment(sketch, "E3.0.5.56", {"start": v(-11, -13) * mm, "end": v(-4, -13) * mm});
            skLineSegment(sketch, "E3.0.5.57", {"start": v(-41, -20) * mm, "end": v(-34, -20) * mm});
            skLineSegment(sketch, "E3.0.5.58", {"start": v(19, -20) * mm, "end": v(26, -20) * mm});
            skPoint(sketch, "E3.0.5.59", {"position": v(-37.5, -16.5) * mm});
            skLineSegment(sketch, "E3.0.5.60", {"start": v(86, -20) * mm, "end": v(71, -20) * mm, "construction": true});
            skLineSegment(sketch, "E3.0.6.0", {"start": v(-49, -31) * mm, "end": v(-49, -24) * mm});
            skLineSegment(sketch, "E3.0.6.1", {"start": v(4, -31) * mm, "end": v(11, -31) * mm});
            skLineSegment(sketch, "E3.0.6.2", {"start": v(-56, -31) * mm, "end": v(-49, -31) * mm});
            skLineSegment(sketch, "E3.0.6.3", {"start": v(-11, -31) * mm, "end": v(-4, -31) * mm});
            skLineSegment(sketch, "E3.0.6.4", {"start": v(-71, -31) * mm, "end": v(-64, -31) * mm});
            skPoint(sketch, "E3.0.6.5", {"position": v(7.5, -27.5) * mm});
            skLineSegment(sketch, "E3.0.6.6", {"start": v(-26, -31) * mm, "end": v(-26, -24) * mm});
            skLineSegment(sketch, "E3.0.6.7", {"start": v(11, -31) * mm, "end": v(11, -24) * mm});
            skPoint(sketch, "E3.0.6.8", {"position": v(-52.5, -27.5) * mm});
            skLineSegment(sketch, "E3.0.6.9", {"start": v(-86, -31) * mm, "end": v(-86, -24) * mm});
            skLineSegment(sketch, "E3.0.6.10", {"start": v(-34, -31) * mm, "end": v(-34, -24) * mm});
            skLineSegment(sketch, "E3.0.6.11", {"start": v(26, -31) * mm, "end": v(26, -24) * mm});
            skPoint(sketch, "E3.0.6.12", {"position": v(37.5, -27.5) * mm});
            skLineSegment(sketch, "E3.0.6.13", {"start": v(-79, -31) * mm, "end": v(-79, -24) * mm});
            skLineSegment(sketch, "E3.0.6.14", {"start": v(-19, -31) * mm, "end": v(-19, -24) * mm});
            skPoint(sketch, "E3.0.6.15", {"position": v(-82.5, -27.5) * mm});
            skPoint(sketch, "E3.0.6.16", {"position": v(52.5, -27.5) * mm});
            skLineSegment(sketch, "E3.0.6.17", {"start": v(-64, -31) * mm, "end": v(-64, -24) * mm});
            skLineSegment(sketch, "E3.0.6.18", {"start": v(-4, -31) * mm, "end": v(-4, -24) * mm});
            skLineSegment(sketch, "E3.0.6.19", {"start": v(-56, -31) * mm, "end": v(-56, -24) * mm});
            skLineSegment(sketch, "E3.0.6.20", {"start": v(-26, -24) * mm, "end": v(-19, -24) * mm});
            skLineSegment(sketch, "E3.0.6.21", {"start": v(4, -31) * mm, "end": v(4, -24) * mm});
            skPoint(sketch, "E3.0.6.22", {"position": v(-67.5, -27.5) * mm});
            skLineSegment(sketch, "E3.0.6.23", {"start": v(-86, -24) * mm, "end": v(-79, -24) * mm});
            skLineSegment(sketch, "E3.0.6.24", {"start": v(-41, -31) * mm, "end": v(-41, -24) * mm});
            skLineSegment(sketch, "E3.0.6.25", {"start": v(19, -31) * mm, "end": v(19, -24) * mm});
            skPoint(sketch, "E3.0.6.26", {"position": v(-7.5, -27.5) * mm});
            skPoint(sketch, "E3.0.6.27", {"position": v(22.5, -27.5) * mm});
            skLineSegment(sketch, "E3.0.6.28", {"start": v(34, -31) * mm, "end": v(34, -24) * mm});
            skLineSegment(sketch, "E3.0.6.29", {"start": v(34, -24) * mm, "end": v(41, -24) * mm});
            skLineSegment(sketch, "E3.0.6.30", {"start": v(34, -31) * mm, "end": v(41, -31) * mm});
            skPoint(sketch, "E3.0.6.31", {"position": v(82.5, -27.5) * mm});
            skLineSegment(sketch, "E3.0.6.32", {"start": v(79, -31) * mm, "end": v(86, -31) * mm});
            skLineSegment(sketch, "E3.0.6.33", {"start": v(79, -24) * mm, "end": v(86, -24) * mm});
            skLineSegment(sketch, "E3.0.6.34", {"start": v(79, -31) * mm, "end": v(79, -24) * mm});
            skLineSegment(sketch, "E3.0.6.35", {"start": v(86, -31) * mm, "end": v(86, -24) * mm});
            skLineSegment(sketch, "E3.0.6.36", {"start": v(71, -31) * mm, "end": v(71, -24) * mm});
            skLineSegment(sketch, "E3.0.6.37", {"start": v(64, -31) * mm, "end": v(64, -24) * mm});
            skLineSegment(sketch, "E3.0.6.38", {"start": v(64, -24) * mm, "end": v(71, -24) * mm});
            skLineSegment(sketch, "E3.0.6.39", {"start": v(64, -31) * mm, "end": v(71, -31) * mm});
            skLineSegment(sketch, "E3.0.6.40", {"start": v(56, -31) * mm, "end": v(56, -24) * mm});
            skLineSegment(sketch, "E3.0.6.41", {"start": v(49, -31) * mm, "end": v(49, -24) * mm});
            skLineSegment(sketch, "E3.0.6.42", {"start": v(49, -24) * mm, "end": v(56, -24) * mm});
            skLineSegment(sketch, "E3.0.6.43", {"start": v(49, -31) * mm, "end": v(56, -31) * mm});
            skLineSegment(sketch, "E3.0.6.44", {"start": v(-71, -31) * mm, "end": v(-71, -24) * mm});
            skLineSegment(sketch, "E3.0.6.45", {"start": v(-11, -31) * mm, "end": v(-11, -24) * mm});
            skLineSegment(sketch, "E3.0.6.46", {"start": v(41, -31) * mm, "end": v(41, -24) * mm});
            skLineSegment(sketch, "E3.0.6.47", {"start": v(-26, -31) * mm, "end": v(-19, -31) * mm});
            skLineSegment(sketch, "E3.0.6.48", {"start": v(-56, -24) * mm, "end": v(-49, -24) * mm});
            skLineSegment(sketch, "E3.0.6.49", {"start": v(4, -24) * mm, "end": v(11, -24) * mm});
            skLineSegment(sketch, "E3.0.6.50", {"start": v(-86, -31) * mm, "end": v(-79, -31) * mm});
            skLineSegment(sketch, "E3.0.6.51", {"start": v(-41, -24) * mm, "end": v(-34, -24) * mm});
            skLineSegment(sketch, "E3.0.6.52", {"start": v(19, -24) * mm, "end": v(26, -24) * mm});
            skPoint(sketch, "E3.0.6.53", {"position": v(-22.5, -27.5) * mm});
            skPoint(sketch, "E3.0.6.54", {"position": v(67.5, -27.5) * mm});
            skLineSegment(sketch, "E3.0.6.55", {"start": v(-71, -24) * mm, "end": v(-64, -24) * mm});
            skLineSegment(sketch, "E3.0.6.56", {"start": v(-11, -24) * mm, "end": v(-4, -24) * mm});
            skLineSegment(sketch, "E3.0.6.57", {"start": v(-41, -31) * mm, "end": v(-34, -31) * mm});
            skLineSegment(sketch, "E3.0.6.58", {"start": v(19, -31) * mm, "end": v(26, -31) * mm});
            skPoint(sketch, "E3.0.6.59", {"position": v(-37.5, -27.5) * mm});
            skLineSegment(sketch, "E3.0.6.60", {"start": v(86, -31) * mm, "end": v(71, -31) * mm, "construction": true});
            skLineSegment(sketch, "E3.0.7.0", {"start": v(-49, -42) * mm, "end": v(-49, -35) * mm});
            skLineSegment(sketch, "E3.0.7.1", {"start": v(4, -42) * mm, "end": v(11, -42) * mm});
            skLineSegment(sketch, "E3.0.7.2", {"start": v(-56, -42) * mm, "end": v(-49, -42) * mm});
            skLineSegment(sketch, "E3.0.7.3", {"start": v(-11, -42) * mm, "end": v(-4, -42) * mm});
            skLineSegment(sketch, "E3.0.7.4", {"start": v(-71, -42) * mm, "end": v(-64, -42) * mm});
            skPoint(sketch, "E3.0.7.5", {"position": v(7.5, -38.5) * mm});
            skLineSegment(sketch, "E3.0.7.6", {"start": v(-26, -42) * mm, "end": v(-26, -35) * mm});
            skLineSegment(sketch, "E3.0.7.7", {"start": v(11, -42) * mm, "end": v(11, -35) * mm});
            skPoint(sketch, "E3.0.7.8", {"position": v(-52.5, -38.5) * mm});
            skLineSegment(sketch, "E3.0.7.9", {"start": v(-86, -42) * mm, "end": v(-86, -35) * mm});
            skLineSegment(sketch, "E3.0.7.10", {"start": v(-34, -42) * mm, "end": v(-34, -35) * mm});
            skLineSegment(sketch, "E3.0.7.11", {"start": v(26, -42) * mm, "end": v(26, -35) * mm});
            skPoint(sketch, "E3.0.7.12", {"position": v(37.5, -38.5) * mm});
            skLineSegment(sketch, "E3.0.7.13", {"start": v(-79, -42) * mm, "end": v(-79, -35) * mm});
            skLineSegment(sketch, "E3.0.7.14", {"start": v(-19, -42) * mm, "end": v(-19, -35) * mm});
            skPoint(sketch, "E3.0.7.15", {"position": v(-82.5, -38.5) * mm});
            skPoint(sketch, "E3.0.7.16", {"position": v(52.5, -38.5) * mm});
            skLineSegment(sketch, "E3.0.7.17", {"start": v(-64, -42) * mm, "end": v(-64, -35) * mm});
            skLineSegment(sketch, "E3.0.7.18", {"start": v(-4, -42) * mm, "end": v(-4, -35) * mm});
            skLineSegment(sketch, "E3.0.7.19", {"start": v(-56, -42) * mm, "end": v(-56, -35) * mm});
            skLineSegment(sketch, "E3.0.7.20", {"start": v(-26, -35) * mm, "end": v(-19, -35) * mm});
            skLineSegment(sketch, "E3.0.7.21", {"start": v(4, -42) * mm, "end": v(4, -35) * mm});
            skPoint(sketch, "E3.0.7.22", {"position": v(-67.5, -38.5) * mm});
            skLineSegment(sketch, "E3.0.7.23", {"start": v(-86, -35) * mm, "end": v(-79, -35) * mm});
            skLineSegment(sketch, "E3.0.7.24", {"start": v(-41, -42) * mm, "end": v(-41, -35) * mm});
            skLineSegment(sketch, "E3.0.7.25", {"start": v(19, -42) * mm, "end": v(19, -35) * mm});
            skPoint(sketch, "E3.0.7.26", {"position": v(-7.5, -38.5) * mm});
            skPoint(sketch, "E3.0.7.27", {"position": v(22.5, -38.5) * mm});
            skLineSegment(sketch, "E3.0.7.28", {"start": v(34, -42) * mm, "end": v(34, -35) * mm});
            skLineSegment(sketch, "E3.0.7.29", {"start": v(34, -35) * mm, "end": v(41, -35) * mm});
            skLineSegment(sketch, "E3.0.7.30", {"start": v(34, -42) * mm, "end": v(41, -42) * mm});
            skPoint(sketch, "E3.0.7.31", {"position": v(82.5, -38.5) * mm});
            skLineSegment(sketch, "E3.0.7.32", {"start": v(79, -42) * mm, "end": v(86, -42) * mm});
            skLineSegment(sketch, "E3.0.7.33", {"start": v(79, -35) * mm, "end": v(86, -35) * mm});
            skLineSegment(sketch, "E3.0.7.34", {"start": v(79, -42) * mm, "end": v(79, -35) * mm});
            skLineSegment(sketch, "E3.0.7.35", {"start": v(86, -42) * mm, "end": v(86, -35) * mm});
            skLineSegment(sketch, "E3.0.7.36", {"start": v(71, -42) * mm, "end": v(71, -35) * mm});
            skLineSegment(sketch, "E3.0.7.37", {"start": v(64, -42) * mm, "end": v(64, -35) * mm});
            skLineSegment(sketch, "E3.0.7.38", {"start": v(64, -35) * mm, "end": v(71, -35) * mm});
            skLineSegment(sketch, "E3.0.7.39", {"start": v(64, -42) * mm, "end": v(71, -42) * mm});
            skLineSegment(sketch, "E3.0.7.40", {"start": v(56, -42) * mm, "end": v(56, -35) * mm});
            skLineSegment(sketch, "E3.0.7.41", {"start": v(49, -42) * mm, "end": v(49, -35) * mm});
            skLineSegment(sketch, "E3.0.7.42", {"start": v(49, -35) * mm, "end": v(56, -35) * mm});
            skLineSegment(sketch, "E3.0.7.43", {"start": v(49, -42) * mm, "end": v(56, -42) * mm});
            skLineSegment(sketch, "E3.0.7.44", {"start": v(-71, -42) * mm, "end": v(-71, -35) * mm});
            skLineSegment(sketch, "E3.0.7.45", {"start": v(-11, -42) * mm, "end": v(-11, -35) * mm});
            skLineSegment(sketch, "E3.0.7.46", {"start": v(41, -42) * mm, "end": v(41, -35) * mm});
            skLineSegment(sketch, "E3.0.7.47", {"start": v(-26, -42) * mm, "end": v(-19, -42) * mm});
            skLineSegment(sketch, "E3.0.7.48", {"start": v(-56, -35) * mm, "end": v(-49, -35) * mm});
            skLineSegment(sketch, "E3.0.7.49", {"start": v(4, -35) * mm, "end": v(11, -35) * mm});
            skLineSegment(sketch, "E3.0.7.50", {"start": v(-86, -42) * mm, "end": v(-79, -42) * mm});
            skLineSegment(sketch, "E3.0.7.51", {"start": v(-41, -35) * mm, "end": v(-34, -35) * mm});
            skLineSegment(sketch, "E3.0.7.52", {"start": v(19, -35) * mm, "end": v(26, -35) * mm});
            skPoint(sketch, "E3.0.7.53", {"position": v(-22.5, -38.5) * mm});
            skPoint(sketch, "E3.0.7.54", {"position": v(67.5, -38.5) * mm});
            skLineSegment(sketch, "E3.0.7.55", {"start": v(-71, -35) * mm, "end": v(-64, -35) * mm});
            skLineSegment(sketch, "E3.0.7.56", {"start": v(-11, -35) * mm, "end": v(-4, -35) * mm});
            skLineSegment(sketch, "E3.0.7.57", {"start": v(-41, -42) * mm, "end": v(-34, -42) * mm});
            skLineSegment(sketch, "E3.0.7.58", {"start": v(19, -42) * mm, "end": v(26, -42) * mm});
            skPoint(sketch, "E3.0.7.59", {"position": v(-37.5, -38.5) * mm});
            skLineSegment(sketch, "E3.0.7.60", {"start": v(86, -42) * mm, "end": v(71, -42) * mm, "construction": true});
            skLineSegment(sketch, "E3.direction1", {"start": v(-49, 35) * mm, "end": v(-24, 35) * mm, "construction": true});
            skLineSegment(sketch, "E3.direction2", {"start": v(-49, 35) * mm, "end": v(-49, 24) * mm, "construction": true});
            skSolve(sketch);
        }
        {
            var Q0;
            Q0 = qSketchRegion(id + "F2", true);
            extrude(context, id + "F3", {"entities" : qUnion([Q0]), "operationType" : NewBodyOperationType.REMOVE, "endBound" : BoundingType.THROUGH_ALL, "oppositeDirection" : true, "depth" : 25 * mm});
        }
        {
            var Q0;
            Q0=makeQuery(id+"F1.opExtrude","SWEPT_EDGE",EDGE,{"disambiguationData":[OSD([sQuery(id+"F0.wireOp",EDGE,"E0.rect.top"),sQuery(id+"F0.wireOp",EDGE,"E0.rect.right")])]});
            chamfer(context, id + "F4", {"entities" : qUnion([Q0]), "width" : 10 * mm, "tangentPropagation" : true});
        }
        {
            var Q0;
            Q0=makeQuery(id+"F1.opExtrude","CAP_EDGE",EDGE,{"disambiguationData":[OSD([sQuery(id+"F0.wireOp",EDGE,"E0.rect.right")])],"isStart":false});
            var Q1;
            Q1=makeQuery(id+"F1.opExtrude","CAP_EDGE",EDGE,{"disambiguationData":[OSD([sQuery(id+"F0.wireOp",EDGE,"E0.rect.bottom")])],"isStart":false});
            var Q2;
            Q2=makeQuery(id+"F1.opExtrude","CAP_EDGE",EDGE,{"disambiguationData":[OSD([sQuery(id+"F0.wireOp",EDGE,"E0.rect.left")])],"isStart":false});
            var Q3;
            Q3=makeQuery(id+"F1.opExtrude","CAP_EDGE",EDGE,{"disambiguationData":[OSD([sQuery(id+"F0.wireOp",EDGE,"E0.rect.top")])],"isStart":false});
            var Q4;
            {var subQ0=sQuery(id+"F0.wireOp",EDGE,"E0.rect.right");var subQ1=sQuery(id+"F0.wireOp",EDGE,"E0.rect.top");Q4=makeQuery(id+"F4.opChamfer","BLEND_EDGE",EDGE,{"blendedFrom":[makeQuery(id+"F1.opExtrude","SWEPT_EDGE",EDGE,{"disambiguationData":[OSD([subQ1,subQ0])]}),makeQuery(id+"F1.opExtrude","CAP_FACE",FACE,{"disambiguationData":[OSD([sQuery(id+"F0.wireOp",EDGE,"E0.rect.bottom"),subQ1,sQuery(id+"F0.wireOp",EDGE,"E0.rect.left"),subQ0])],"isStart":false})],"blendedInto":[makeQuery(id+"F1.opExtrude","CAP_FACE",FACE,{"disambiguationData":[OSD([sQuery(id+"F0.wireOp",EDGE,"E0.rect.bottom"),subQ1,sQuery(id+"F0.wireOp",EDGE,"E0.rect.left"),subQ0])],"isStart":false})]});}
            fillet(context, id + "F5", {"entities" : qUnion([Q0, Q1, Q2, Q3, Q4]), "radius" : 1 * mm, "tangentPropagation" : true, "allowEdgeOverflow" : false});
        }
        {
            var Q0;
            Q0=makeQuery(id+"F1.opExtrude","CAP_EDGE",EDGE,{"disambiguationData":[OSD([sQuery(id+"F0.wireOp",EDGE,"E0.rect.right")])],"isStart":true});
            var Q1;
            Q1=makeQuery(id+"F1.opExtrude","CAP_EDGE",EDGE,{"disambiguationData":[OSD([sQuery(id+"F0.wireOp",EDGE,"E0.rect.bottom")])],"isStart":true});
            var Q2;
            Q2=makeQuery(id+"F1.opExtrude","CAP_EDGE",EDGE,{"disambiguationData":[OSD([sQuery(id+"F0.wireOp",EDGE,"E0.rect.left")])],"isStart":true});
            var Q3;
            Q3=makeQuery(id+"F1.opExtrude","CAP_EDGE",EDGE,{"disambiguationData":[OSD([sQuery(id+"F0.wireOp",EDGE,"E0.rect.top")])],"isStart":true});
            var Q4;
            {var subQ0=sQuery(id+"F0.wireOp",EDGE,"E0.rect.right");var subQ1=sQuery(id+"F0.wireOp",EDGE,"E0.rect.top");var subQ2=makeQuery(id+"F1.opExtrude","CAP_FACE",FACE,{"disambiguationData":[OSD([sQuery(id+"F0.wireOp",EDGE,"E0.rect.bottom"),subQ1,sQuery(id+"F0.wireOp",EDGE,"E0.rect.left"),subQ0])],"isStart":true});Q4=makeQuery(id+"FUhNQVGm88cYsiD_1.boolean.opBoolean","SPLIT",EDGE,{"disambiguationData":[TD([makeQuery(id+"F1.opExtrude","SWEPT_FACE",FACE,{"disambiguationData":[OSD([subQ0])]})])],"derivedFrom":makeQuery(id+"F4.opChamfer","BLEND_EDGE",EDGE,{"blendedFrom":[makeQuery(id+"F1.opExtrude","SWEPT_EDGE",EDGE,{"disambiguationData":[OSD([subQ1,subQ0])]}),subQ2],"blendedInto":[subQ2]})});}
            fillet(context, id + "F6", {"entities" : qUnion([Q0, Q1, Q2, Q3, Q4]), "radius" : 1 * mm, "tangentPropagation" : true, "allowEdgeOverflow" : false});
        }
        {
            var Q0;
            Q0=makeQuery(id+"F1.opExtrude","CAP_FACE",FACE,{"disambiguationData":[OSD([sQuery(id+"F0.wireOp",EDGE,"E0.rect.bottom"),sQuery(id+"F0.wireOp",EDGE,"E0.rect.top"),sQuery(id+"F0.wireOp",EDGE,"E0.rect.left"),sQuery(id+"F0.wireOp",EDGE,"E0.rect.right")])],"isStart":false});
            var sketch = newSketch(context, id + "F7", { "sketchPlane" : qUnion([Q0])});
            skCircle(sketch, "E4", {"center": v(82.5, 38.5) * mm, "radius": 5 * mm});
            skLineSegment(sketch, "E5", {"start": v(79, 42) * mm, "end": v(86, 35) * mm, "construction": true});
            skLineSegment(sketch, "E6", {"start": v(79, 35) * mm, "end": v(86, 42) * mm, "construction": true});
            skCircle(sketch, "E7.0.1.0", {"center": v(82.5, 27.5) * mm, "radius": 5 * mm});
            skCircle(sketch, "E7.1.0.0", {"center": v(67.5, 38.5) * mm, "radius": 5 * mm});
            skCircle(sketch, "E7.1.1.0", {"center": v(67.5, 27.5) * mm, "radius": 5 * mm});
            skCircle(sketch, "E7.2.0.0", {"center": v(52.5, 38.5) * mm, "radius": 5 * mm});
            skCircle(sketch, "E7.2.1.0", {"center": v(52.5, 27.5) * mm, "radius": 5 * mm});
            skLineSegment(sketch, "E7.direction1", {"start": v(82.5, 38.5) * mm, "end": v(67.5, 38.5) * mm, "construction": true});
            skLineSegment(sketch, "E7.direction2", {"start": v(82.5, 38.5) * mm, "end": v(82.5, 27.5) * mm, "construction": true});
            skCircle(sketch, "E8.0.0.2", {"center": v(82.5, 16.5) * mm, "radius": 5 * mm});
            skCircle(sketch, "E8.0.0.3", {"center": v(82.5, 5.5) * mm, "radius": 5 * mm});
            skCircle(sketch, "E8.0.0.4", {"center": v(82.5, -5.5) * mm, "radius": 5 * mm});
            skCircle(sketch, "E8.0.0.5", {"center": v(82.5, -16.5) * mm, "radius": 5 * mm});
            skCircle(sketch, "E8.0.0.6", {"center": v(82.5, -27.5) * mm, "radius": 5 * mm});
            skCircle(sketch, "E8.0.0.7", {"center": v(82.5, -38.5) * mm, "radius": 5 * mm});
            skCircle(sketch, "E8.0.1.2", {"center": v(67.5, 16.5) * mm, "radius": 5 * mm});
            skCircle(sketch, "E8.0.1.3", {"center": v(67.5, 5.5) * mm, "radius": 5 * mm});
            skCircle(sketch, "E8.0.1.4", {"center": v(67.5, -5.5) * mm, "radius": 5 * mm});
            skCircle(sketch, "E8.0.1.5", {"center": v(67.5, -16.5) * mm, "radius": 5 * mm});
            skCircle(sketch, "E8.0.1.6", {"center": v(67.5, -27.5) * mm, "radius": 5 * mm});
            skCircle(sketch, "E8.0.1.7", {"center": v(67.5, -38.5) * mm, "radius": 5 * mm});
            skCircle(sketch, "E8.0.2.2", {"center": v(52.5, 16.5) * mm, "radius": 5 * mm});
            skCircle(sketch, "E8.0.2.3", {"center": v(52.5, 5.5) * mm, "radius": 5 * mm});
            skCircle(sketch, "E8.0.2.4", {"center": v(52.5, -5.5) * mm, "radius": 5 * mm});
            skCircle(sketch, "E8.0.2.5", {"center": v(52.5, -16.5) * mm, "radius": 5 * mm});
            skCircle(sketch, "E8.0.2.6", {"center": v(52.5, -27.5) * mm, "radius": 5 * mm});
            skCircle(sketch, "E8.0.2.7", {"center": v(52.5, -38.5) * mm, "radius": 5 * mm});
            skCircle(sketch, "E9.0.3.0", {"center": v(37.5, 38.5) * mm, "radius": 5 * mm});
            skCircle(sketch, "E9.0.3.1", {"center": v(37.5, 27.5) * mm, "radius": 5 * mm});
            skCircle(sketch, "E9.0.3.2", {"center": v(37.5, 16.5) * mm, "radius": 5 * mm});
            skCircle(sketch, "E9.0.3.3", {"center": v(37.5, 5.5) * mm, "radius": 5 * mm});
            skCircle(sketch, "E9.0.3.4", {"center": v(37.5, -5.5) * mm, "radius": 5 * mm});
            skCircle(sketch, "E9.0.3.5", {"center": v(37.5, -16.5) * mm, "radius": 5 * mm});
            skCircle(sketch, "E9.0.3.6", {"center": v(37.5, -27.5) * mm, "radius": 5 * mm});
            skCircle(sketch, "E9.0.3.7", {"center": v(37.5, -38.5) * mm, "radius": 5 * mm});
            skCircle(sketch, "E9.0.4.0", {"center": v(22.5, 38.5) * mm, "radius": 5 * mm});
            skCircle(sketch, "E9.0.4.1", {"center": v(22.5, 27.5) * mm, "radius": 5 * mm});
            skCircle(sketch, "E9.0.4.2", {"center": v(22.5, 16.5) * mm, "radius": 5 * mm});
            skCircle(sketch, "E9.0.4.3", {"center": v(22.5, 5.5) * mm, "radius": 5 * mm});
            skCircle(sketch, "E9.0.4.4", {"center": v(22.5, -5.5) * mm, "radius": 5 * mm});
            skCircle(sketch, "E9.0.4.5", {"center": v(22.5, -16.5) * mm, "radius": 5 * mm});
            skCircle(sketch, "E9.0.4.6", {"center": v(22.5, -27.5) * mm, "radius": 5 * mm});
            skCircle(sketch, "E9.0.4.7", {"center": v(22.5, -38.5) * mm, "radius": 5 * mm});
            skCircle(sketch, "E9.0.5.0", {"center": v(7.5, 38.5) * mm, "radius": 5 * mm});
            skCircle(sketch, "E9.0.5.1", {"center": v(7.5, 27.5) * mm, "radius": 5 * mm});
            skCircle(sketch, "E9.0.5.2", {"center": v(7.5, 16.5) * mm, "radius": 5 * mm});
            skCircle(sketch, "E9.0.5.3", {"center": v(7.5, 5.5) * mm, "radius": 5 * mm});
            skCircle(sketch, "E9.0.5.4", {"center": v(7.5, -5.5) * mm, "radius": 5 * mm});
            skCircle(sketch, "E9.0.5.5", {"center": v(7.5, -16.5) * mm, "radius": 5 * mm});
            skCircle(sketch, "E9.0.5.6", {"center": v(7.5, -27.5) * mm, "radius": 5 * mm});
            skCircle(sketch, "E9.0.5.7", {"center": v(7.5, -38.5) * mm, "radius": 5 * mm});
            skCircle(sketch, "E9.0.6.0", {"center": v(-7.5, 38.5) * mm, "radius": 5 * mm});
            skCircle(sketch, "E9.0.6.1", {"center": v(-7.5, 27.5) * mm, "radius": 5 * mm});
            skCircle(sketch, "E9.0.6.2", {"center": v(-7.5, 16.5) * mm, "radius": 5 * mm});
            skCircle(sketch, "E9.0.6.3", {"center": v(-7.5, 5.5) * mm, "radius": 5 * mm});
            skCircle(sketch, "E9.0.6.4", {"center": v(-7.5, -5.5) * mm, "radius": 5 * mm});
            skCircle(sketch, "E9.0.6.5", {"center": v(-7.5, -16.5) * mm, "radius": 5 * mm});
            skCircle(sketch, "E9.0.6.6", {"center": v(-7.5, -27.5) * mm, "radius": 5 * mm});
            skCircle(sketch, "E9.0.6.7", {"center": v(-7.5, -38.5) * mm, "radius": 5 * mm});
            skCircle(sketch, "E9.0.7.0", {"center": v(-22.5, 38.5) * mm, "radius": 5 * mm});
            skCircle(sketch, "E9.0.7.1", {"center": v(-22.5, 27.5) * mm, "radius": 5 * mm});
            skCircle(sketch, "E9.0.7.2", {"center": v(-22.5, 16.5) * mm, "radius": 5 * mm});
            skCircle(sketch, "E9.0.7.3", {"center": v(-22.5, 5.5) * mm, "radius": 5 * mm});
            skCircle(sketch, "E9.0.7.4", {"center": v(-22.5, -5.5) * mm, "radius": 5 * mm});
            skCircle(sketch, "E9.0.7.5", {"center": v(-22.5, -16.5) * mm, "radius": 5 * mm});
            skCircle(sketch, "E9.0.7.6", {"center": v(-22.5, -27.5) * mm, "radius": 5 * mm});
            skCircle(sketch, "E9.0.7.7", {"center": v(-22.5, -38.5) * mm, "radius": 5 * mm});
            skCircle(sketch, "E9.0.8.0", {"center": v(-37.5, 38.5) * mm, "radius": 5 * mm});
            skCircle(sketch, "E9.0.8.1", {"center": v(-37.5, 27.5) * mm, "radius": 5 * mm});
            skCircle(sketch, "E9.0.8.2", {"center": v(-37.5, 16.5) * mm, "radius": 5 * mm});
            skCircle(sketch, "E9.0.8.3", {"center": v(-37.5, 5.5) * mm, "radius": 5 * mm});
            skCircle(sketch, "E9.0.8.4", {"center": v(-37.5, -5.5) * mm, "radius": 5 * mm});
            skCircle(sketch, "E9.0.8.5", {"center": v(-37.5, -16.5) * mm, "radius": 5 * mm});
            skCircle(sketch, "E9.0.8.6", {"center": v(-37.5, -27.5) * mm, "radius": 5 * mm});
            skCircle(sketch, "E9.0.8.7", {"center": v(-37.5, -38.5) * mm, "radius": 5 * mm});
            skCircle(sketch, "E9.0.9.0", {"center": v(-52.5, 38.5) * mm, "radius": 5 * mm});
            skCircle(sketch, "E9.0.9.1", {"center": v(-52.5, 27.5) * mm, "radius": 5 * mm});
            skCircle(sketch, "E9.0.9.2", {"center": v(-52.5, 16.5) * mm, "radius": 5 * mm});
            skCircle(sketch, "E9.0.9.3", {"center": v(-52.5, 5.5) * mm, "radius": 5 * mm});
            skCircle(sketch, "E9.0.9.4", {"center": v(-52.5, -5.5) * mm, "radius": 5 * mm});
            skCircle(sketch, "E9.0.9.5", {"center": v(-52.5, -16.5) * mm, "radius": 5 * mm});
            skCircle(sketch, "E9.0.9.6", {"center": v(-52.5, -27.5) * mm, "radius": 5 * mm});
            skCircle(sketch, "E9.0.9.7", {"center": v(-52.5, -38.5) * mm, "radius": 5 * mm});
            skCircle(sketch, "E9.0.10.0", {"center": v(-67.5, 38.5) * mm, "radius": 5 * mm});
            skCircle(sketch, "E9.0.10.1", {"center": v(-67.5, 27.5) * mm, "radius": 5 * mm});
            skCircle(sketch, "E9.0.10.2", {"center": v(-67.5, 16.5) * mm, "radius": 5 * mm});
            skCircle(sketch, "E9.0.10.3", {"center": v(-67.5, 5.5) * mm, "radius": 5 * mm});
            skCircle(sketch, "E9.0.10.4", {"center": v(-67.5, -5.5) * mm, "radius": 5 * mm});
            skCircle(sketch, "E9.0.10.5", {"center": v(-67.5, -16.5) * mm, "radius": 5 * mm});
            skCircle(sketch, "E9.0.10.6", {"center": v(-67.5, -27.5) * mm, "radius": 5 * mm});
            skCircle(sketch, "E9.0.10.7", {"center": v(-67.5, -38.5) * mm, "radius": 5 * mm});
            skCircle(sketch, "E9.0.11.0", {"center": v(-82.5, 38.5) * mm, "radius": 5 * mm});
            skCircle(sketch, "E9.0.11.1", {"center": v(-82.5, 27.5) * mm, "radius": 5 * mm});
            skCircle(sketch, "E9.0.11.2", {"center": v(-82.5, 16.5) * mm, "radius": 5 * mm});
            skCircle(sketch, "E9.0.11.3", {"center": v(-82.5, 5.5) * mm, "radius": 5 * mm});
            skCircle(sketch, "E9.0.11.4", {"center": v(-82.5, -5.5) * mm, "radius": 5 * mm});
            skCircle(sketch, "E9.0.11.5", {"center": v(-82.5, -16.5) * mm, "radius": 5 * mm});
            skCircle(sketch, "E9.0.11.6", {"center": v(-82.5, -27.5) * mm, "radius": 5 * mm});
            skCircle(sketch, "E9.0.11.7", {"center": v(-82.5, -38.5) * mm, "radius": 5 * mm});
            skSolve(sketch);
        }
        {
            var Q0;
            Q0 = qSketchRegion(id + "F7", true);
            extrude(context, id + "F8", {"entities" : qUnion([Q0]), "operationType" : NewBodyOperationType.REMOVE, "oppositeDirection" : true, "depth" : 1 * mm});
        }
        {
            var Q0;
            Q0=makeQuery(id+"F1.opExtrude","CAP_FACE",FACE,{"disambiguationData":[OSD([sQuery(id+"F0.wireOp",EDGE,"E0.rect.bottom"),sQuery(id+"F0.wireOp",EDGE,"E0.rect.top"),sQuery(id+"F0.wireOp",EDGE,"E0.rect.left"),sQuery(id+"F0.wireOp",EDGE,"E0.rect.right")])],"isStart":true});
            var sketch = newSketch(context, id + "F9", { "sketchPlane" : qUnion([Q0])});
            skLineSegment(sketch, "E10", {"start": v(-95.8, 49) * mm, "end": v(-95.8, 39) * mm});
            skLineSegment(sketch, "E11", {"start": v(-95.8, 39) * mm, "end": v(-85.8, 49) * mm});
            skLineSegment(sketch, "E12", {"start": v(-85.8, 49) * mm, "end": v(-95.8, 49) * mm});
            skLineSegment(sketch, "E13", {"start": v(85.8, 49) * mm, "end": v(95.8, 49) * mm});
            skLineSegment(sketch, "E14", {"start": v(95.8, 49) * mm, "end": v(95.8, 39) * mm});
            skLineSegment(sketch, "E15", {"start": v(95.8, 39) * mm, "end": v(85.8, 49) * mm});
            skLineSegment(sketch, "E16", {"start": v(95.8, -49) * mm, "end": v(95.8, -39) * mm});
            skLineSegment(sketch, "E17", {"start": v(95.8, -39) * mm, "end": v(85.8, -49) * mm});
            skLineSegment(sketch, "E18", {"start": v(85.8, -49) * mm, "end": v(95.8, -49) * mm});
            skLineSegment(sketch, "E19", {"start": v(-95.8, -39.59) * mm, "end": v(-86.39, -49) * mm});
            skLineSegment(sketch, "E20", {"start": v(-86.39, -49) * mm, "end": v(-81.21, -49) * mm});
            skLineSegment(sketch, "E21", {"start": v(-81.21, -49) * mm, "end": v(-95.8, -34.41) * mm});
            skLineSegment(sketch, "E22", {"start": v(-95.8, -34.41) * mm, "end": v(-95.8, -39.59) * mm});
            skSolve(sketch);
        }
        {
            var Q0;
            Q0 = qSketchRegion(id + "F9", true);
            extrude(context, id + "F10", {"entities" : qUnion([Q0]), "operationType" : NewBodyOperationType.ADD, "depth" : 7 * mm});
        }
    });
